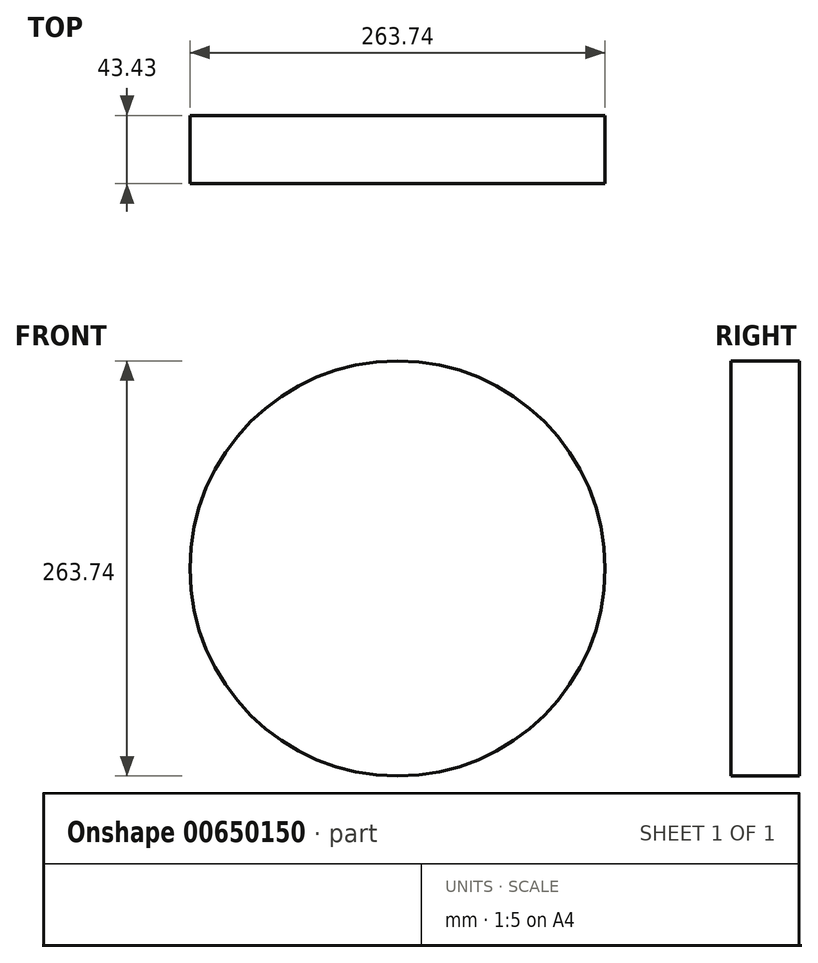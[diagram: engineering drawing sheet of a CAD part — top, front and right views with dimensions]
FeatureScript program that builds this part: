
annotation { "Feature Type Name" : "Feature", "Feature Type Description" : "" }
export const myFeature = defineFeature(function(context is Context, id is Id, definition is map)
    precondition{}
    {
        {
            var Q0;
            Q0=qCreatedBy(makeId("Front.planeOp"),FACE);
            var sketch = newSketch(context, id + "F0", { "sketchPlane" : qUnion([Q0])});
            skCircle(sketch, "E0", {"center": v(0, 0) * mm, "radius": 131.87 * mm});
            skSolve(sketch);
        }
        {
            var Q0;
            Q0=makeQuery(id+"F0.imprint","IMPRINT",FACE,{"disambiguationData":[TD([[makeQuery(id+"F0.imprint","IMPRINT",EDGE,{"derivedFrom":sQuery(id+"F0.wireOp",EDGE,"E0")}),1.0]])]});
            extrude(context, id + "F1", {"entities" : qUnion([Q0]), "oppositeDirection" : true, "depth" : 43.43 * mm, "offsetDistance" : 25.4 * mm});
        }
    });
